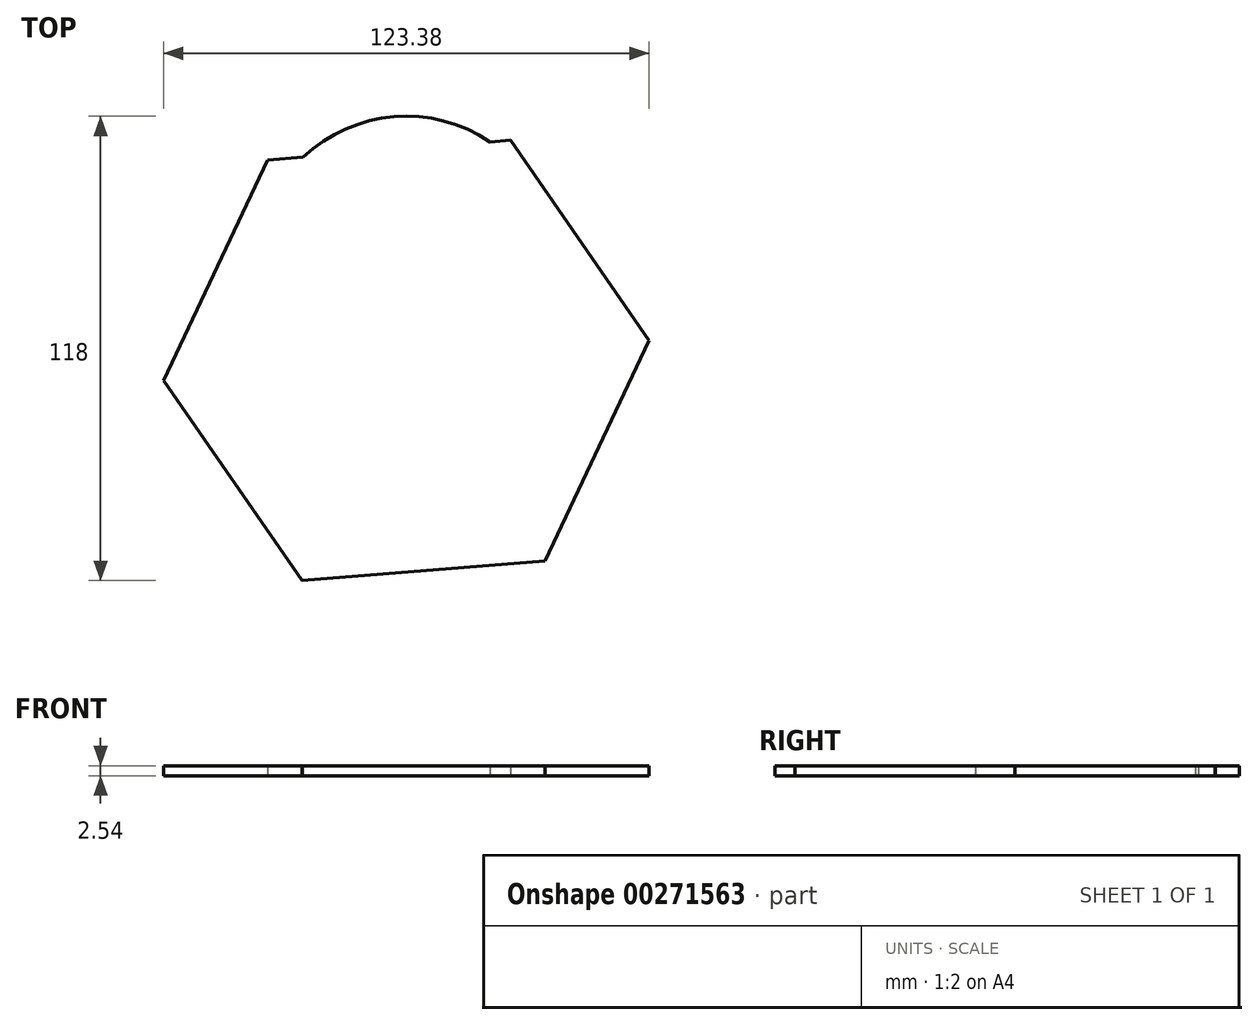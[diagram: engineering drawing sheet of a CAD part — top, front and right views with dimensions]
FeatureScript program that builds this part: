
annotation { "Feature Type Name" : "Feature", "Feature Type Description" : "" }
export const myFeature = defineFeature(function(context is Context, id is Id, definition is map)
    precondition{}
    {
        {
            var Q0;
            Q0=qCreatedBy(makeId("Top.planeOp"),FACE);
            var sketch = newSketch(context, id + "F0", { "sketchPlane" : qUnion([Q0])});
            skCircle(sketch, "E0", {"center": v(0, 0) * mm, "radius": 38.1 * mm});
            skCircle(sketch, "E1.cCircle", {"center": v(0, -23.95) * mm, "radius": 61.9 * mm, "construction": true});
            skLineSegment(sketch, "E1.0", {"start": v(26.47, 32) * mm, "end": v(61.69, -18.9) * mm});
            skLineSegment(sketch, "E1.1", {"start": v(61.69, -18.9) * mm, "end": v(35.22, -74.85) * mm});
            skLineSegment(sketch, "E1.2", {"start": v(35.22, -74.85) * mm, "end": v(-26.47, -79.9) * mm});
            skLineSegment(sketch, "E1.3", {"start": v(-26.47, -79.9) * mm, "end": v(-61.69, -29) * mm});
            skLineSegment(sketch, "E1.4", {"start": v(-61.69, -29) * mm, "end": v(-35.22, 26.94) * mm});
            skLineSegment(sketch, "E1.5", {"start": v(-35.22, 26.94) * mm, "end": v(26.47, 32) * mm});
            skSolve(sketch);
        }
        {
            var Q0;
            Q0 = qSketchRegion(id + "F0", true);
            extrude(context, id + "F1", {"entities" : qUnion([Q0]), "depth" : 2.54 * mm});
        }
    });
